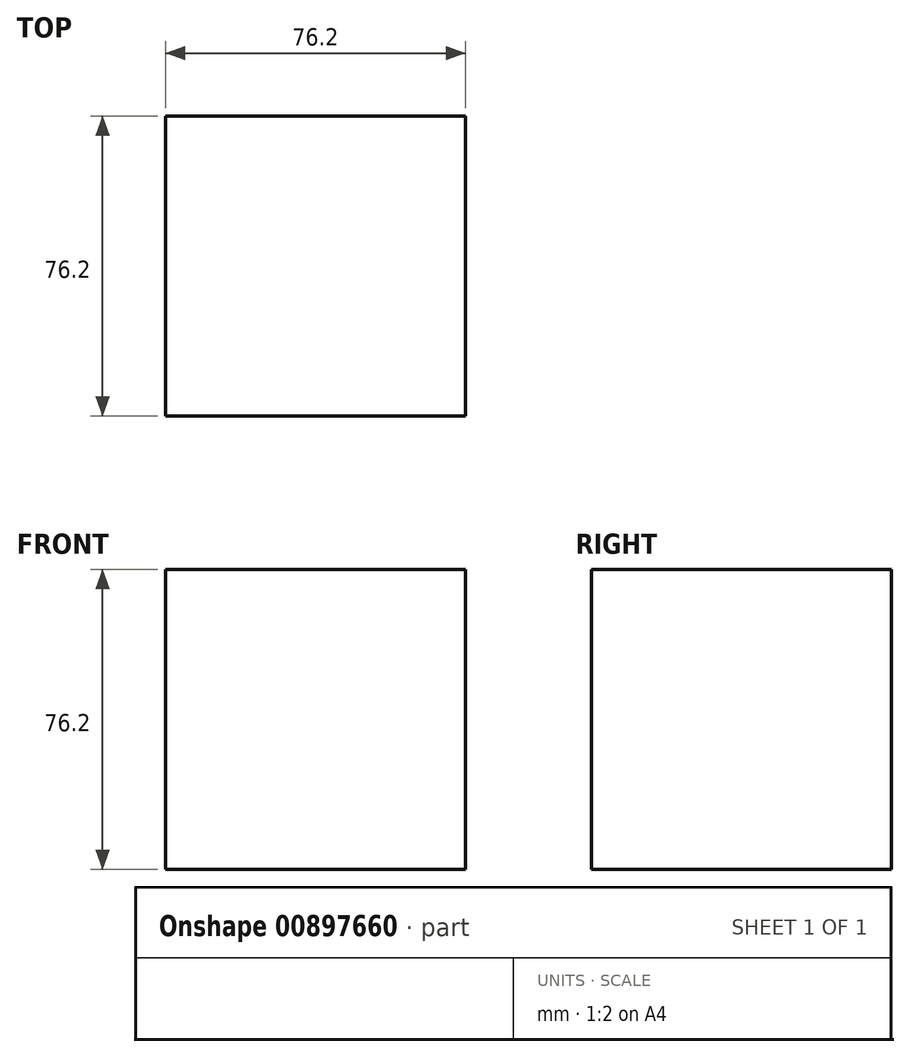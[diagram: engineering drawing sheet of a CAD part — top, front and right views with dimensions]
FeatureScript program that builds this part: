
annotation { "Feature Type Name" : "Feature", "Feature Type Description" : "" }
export const myFeature = defineFeature(function(context is Context, id is Id, definition is map)
    precondition{}
    {
        {
            var Q0;
            Q0=qCreatedBy(makeId("Front.planeOp"),FACE);
            var sketch = newSketch(context, id + "F0", { "sketchPlane" : qUnion([Q0])});
            skLineSegment(sketch, "E0.bottom", {"start": v(38.1, 38.1) * mm, "end": v(-38.1, 38.1) * mm});
            skLineSegment(sketch, "E0.top", {"start": v(38.1, -38.1) * mm, "end": v(-38.1, -38.1) * mm});
            skLineSegment(sketch, "E0.left", {"start": v(38.1, 38.1) * mm, "end": v(38.1, -38.1) * mm});
            skLineSegment(sketch, "E0.right", {"start": v(-38.1, 38.1) * mm, "end": v(-38.1, -38.1) * mm});
            skPoint(sketch, "E0.middle", {"position": v(0, 0) * mm});
            skSolve(sketch);
        }
        {
            var Q0;
            Q0 = qSketchRegion(id + "F0", true);
            var Q1;
            Q1=makeQuery(id+"F0.imprint","IMPRINT",FACE,{"disambiguationData":[TD([[makeQuery(id+"F0.imprint","IMPRINT",EDGE,{"derivedFrom":sQuery(id+"F0.wireOp",EDGE,"E0.bottom")}),1.0]])]});
            extrude(context, id + "F1", {"entities" : qUnion([Q0, Q1]), "depth" : 76.2 * mm, "offsetDistance" : 25.4 * mm});
        }
    });
